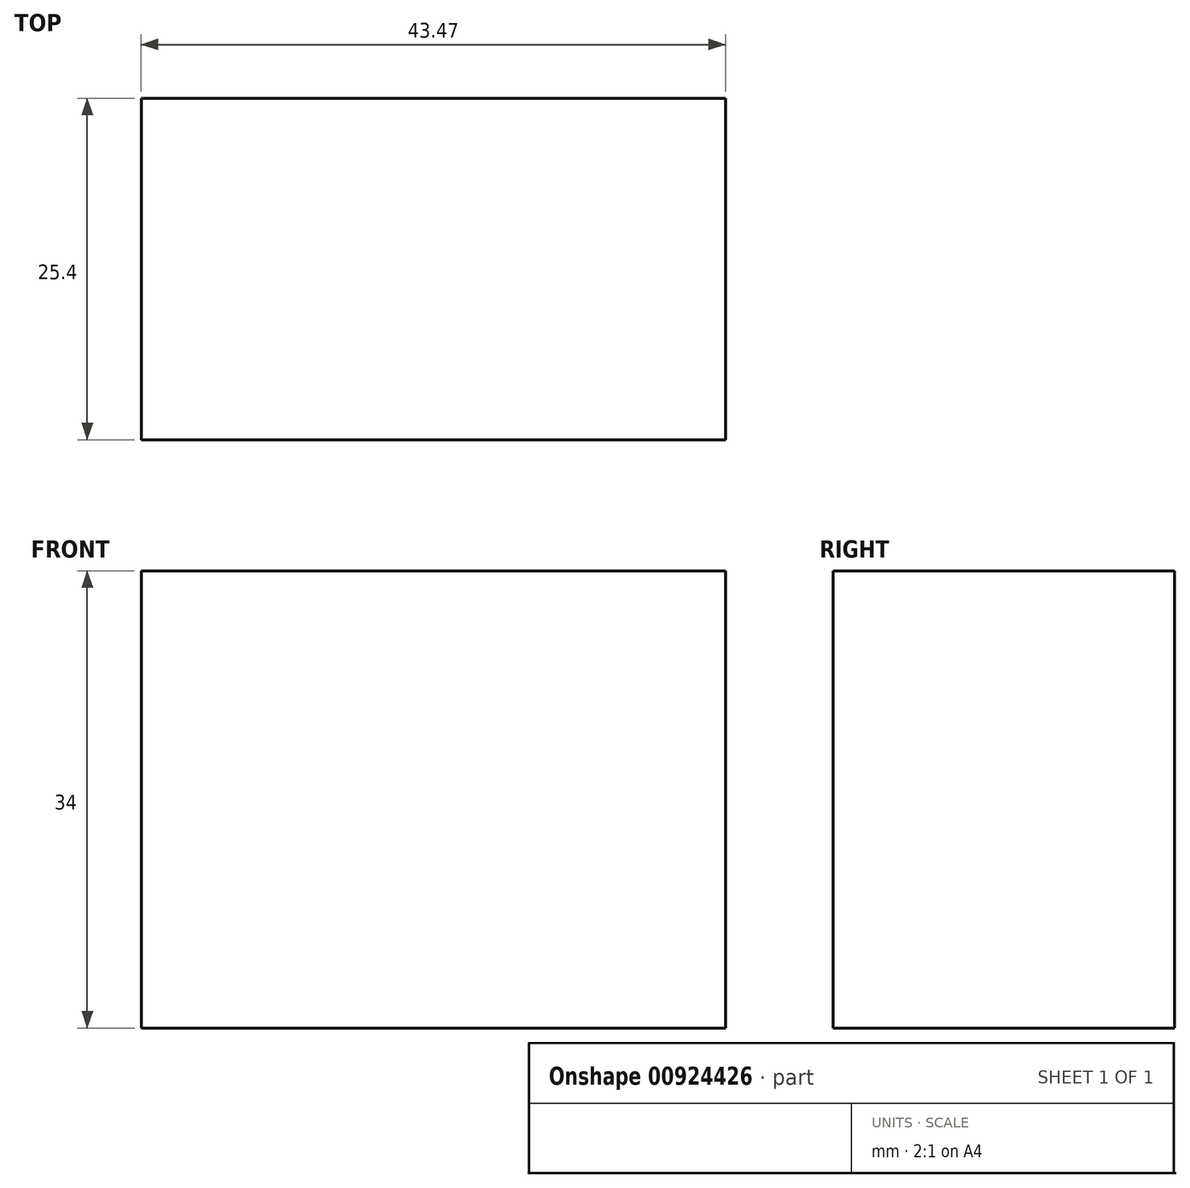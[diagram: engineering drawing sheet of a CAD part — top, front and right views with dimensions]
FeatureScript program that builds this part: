
annotation { "Feature Type Name" : "Feature", "Feature Type Description" : "" }
export const myFeature = defineFeature(function(context is Context, id is Id, definition is map)
    precondition{}
    {
        {
            var Q0;
            Q0=qCreatedBy(makeId("Front.planeOp"),FACE);
            var sketch = newSketch(context, id + "F0", { "sketchPlane" : qUnion([Q0])});
            skLineSegment(sketch, "E0.bottom", {"start": v(-4.8, 0) * mm, "end": v(38.67, 0) * mm});
            skLineSegment(sketch, "E0.top", {"start": v(-4.8, -34) * mm, "end": v(38.67, -34) * mm});
            skLineSegment(sketch, "E0.left", {"start": v(-4.8, 0) * mm, "end": v(-4.8, -34) * mm});
            skLineSegment(sketch, "E0.right", {"start": v(38.67, 0) * mm, "end": v(38.67, -34) * mm});
            skSolve(sketch);
        }
        {
            var Q0;
            Q0=makeQuery(id+"F0.imprint","IMPRINT",FACE,{"disambiguationData":[TD([[makeQuery(id+"F0.imprint","IMPRINT",EDGE,{"derivedFrom":sQuery(id+"F0.wireOp",EDGE,"E0.bottom")}),-1.0]])]});
            extrude(context, id + "F1", {"entities" : qUnion([Q0]), "depth" : 25.4 * mm, "offsetDistance" : 25.4 * mm});
        }
    });
